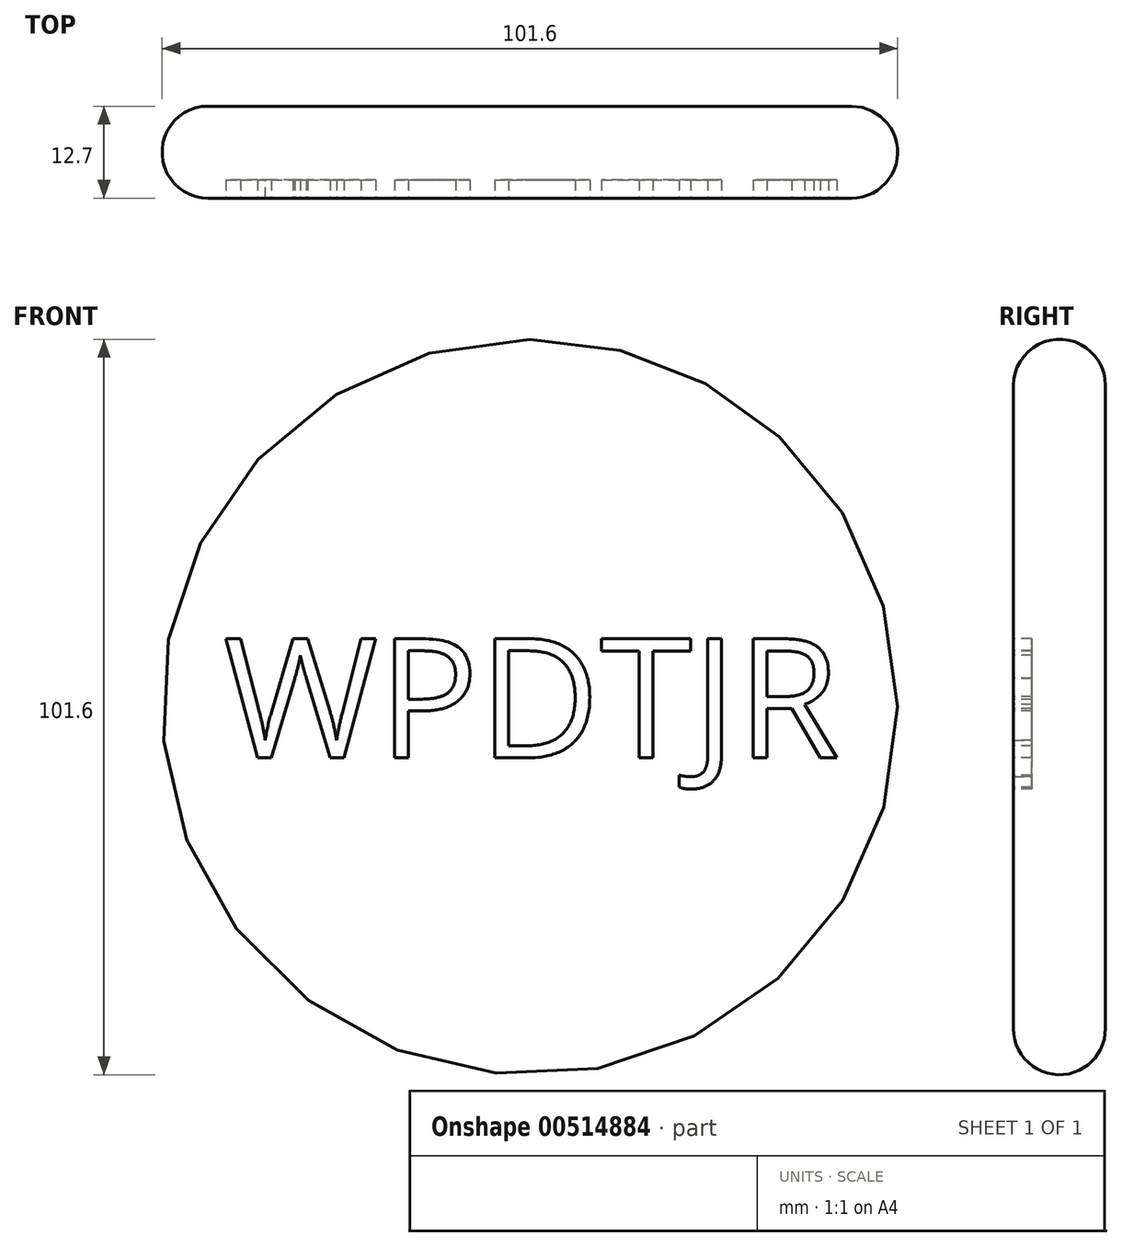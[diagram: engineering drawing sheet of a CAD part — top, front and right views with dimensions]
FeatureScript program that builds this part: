
annotation { "Feature Type Name" : "Feature", "Feature Type Description" : "" }
export const myFeature = defineFeature(function(context is Context, id is Id, definition is map)
    precondition{}
    {
        {
            var Q0;
            Q0=qCreatedBy(makeId("Top.planeOp"),FACE);
            var sketch = newSketch(context, id + "F0", { "sketchPlane" : qUnion([Q0])});
            skLineSegment(sketch, "E0.bottom", {"start": v(-44.45, 12.7) * mm, "end": v(0, 12.7) * mm});
            skLineSegment(sketch, "E0.top", {"start": v(-44.45, 0) * mm, "end": v(0, 0) * mm});
            skLineSegment(sketch, "E0.right", {"start": v(0, 12.7) * mm, "end": v(0, 0) * mm});
            skLineSegment(sketch, "E1", {"start": v(-44.45, 12.7) * mm, "end": v(-44.45, 0) * mm, "construction": true});
            skPoint(sketch, "E2", {"position": v(-44.45, 6.35) * mm});
            skArc(sketch, "E3", {"start": v(-44.45, 12.7) * mm, "mid": v(-50.8, 6.35) * mm, "end": v(-44.45, 0) * mm});
            skPoint(sketch, "E4.orphan", {"position": v(-50.8, 0) * mm});
            skPoint(sketch, "E5.orphan", {"position": v(-25.4, 12.7) * mm});
            skSolve(sketch);
        }
        {
            var Q0;
            Q0=makeQuery(id+"F0.imprint","IMPRINT",FACE,{"disambiguationData":[TD([[makeQuery(id+"F0.imprint","IMPRINT",EDGE,{"derivedFrom":sQuery(id+"F0.wireOp",EDGE,"E0.bottom")}),-1.0]])]});
            var Q1;
            Q1=sQuery(id+"F0.wireOp",EDGE,"E0.right");
            revolve(context, id + "F1", {"entities" : qUnion([Q0]), "axis" : qUnion([Q1]), "revolveType" : RevolveType.FULL});
        }
        {
            var Q0;
            Q0=makeQuery(id+"F1.opRevolve","SWEPT_FACE",FACE,{"disambiguationData":[OSD([sQuery(id+"F0.wireOp",EDGE,"E0.top")])]});
            var sketch = newSketch(context, id + "F2", { "sketchPlane" : qUnion([Q0])});
            skText(sketch, "E6", { "text": "WPDTJR\n", "fontName": "OpenSans-Regular.ttf"});
            const initialGuessF2  = {"E6": [-0.04226, -0.00702, 1, 0, 0.01657]};
            skSetInitialGuess(sketch, initialGuessF2);
            skSolve(sketch);
        }
        {
            var Q0;
            Q0 = qSketchRegion(id + "F2", true);
            extrude(context, id + "F3", {"entities" : qUnion([Q0]), "operationType" : NewBodyOperationType.REMOVE, "oppositeDirection" : true, "depth" : 2.54 * mm, "offsetDistance" : 25.4 * mm});
        }
    });
